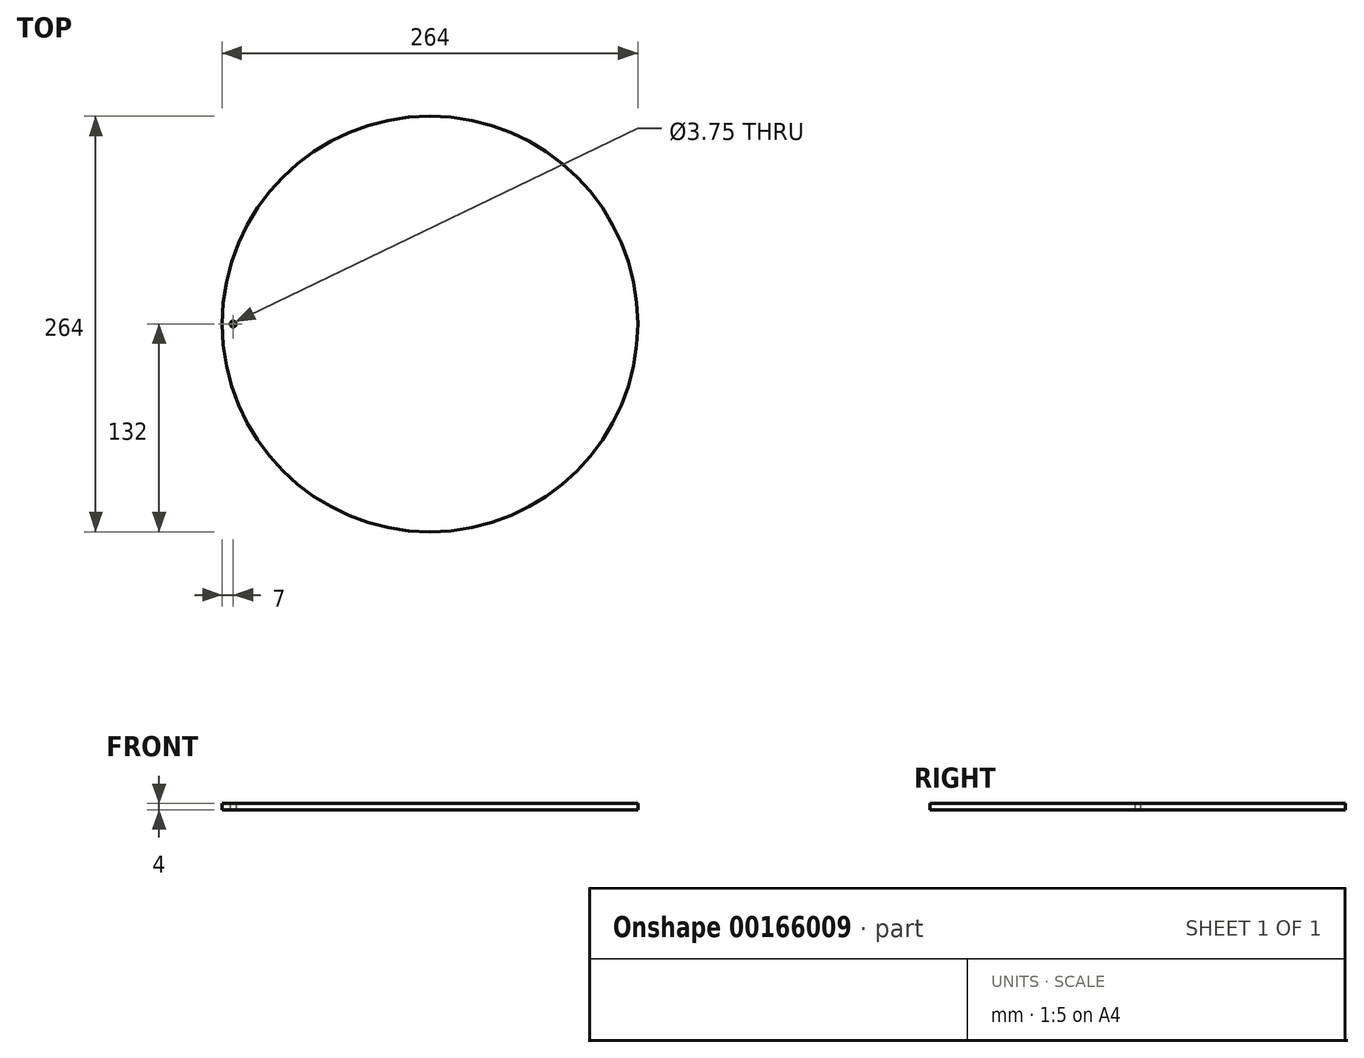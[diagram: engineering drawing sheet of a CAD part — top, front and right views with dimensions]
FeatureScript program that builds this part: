
annotation { "Feature Type Name" : "Feature", "Feature Type Description" : "" }
export const myFeature = defineFeature(function(context is Context, id is Id, definition is map)
    precondition{}
    {
        {
            var Q0;
            Q0=qCreatedBy(makeId("Top.planeOp"),FACE);
            var sketch = newSketch(context, id + "F0", { "sketchPlane" : qUnion([Q0])});
            skCircle(sketch, "E0", {"center": v(0, 0) * mm, "radius": 132 * mm});
            skLineSegment(sketch, "E1", {"start": v(0, 0) * mm, "end": v(-125, 0) * mm, "construction": true});
            skCircle(sketch, "E2", {"center": v(-125, 0) * mm, "radius": 1.88 * mm});
            skSolve(sketch);
        }
        {
            var Q0;
            Q0=makeQuery(id+"F0.imprint","IMPRINT",FACE,{"disambiguationData":[TD([[makeQuery(id+"F0.imprint","IMPRINT",EDGE,{"derivedFrom":sQuery(id+"F0.wireOp",EDGE,"E0")}),1.0]])]});
            extrude(context, id + "F1", {"entities" : qUnion([Q0]), "depth" : 4 * mm});
        }
    });
